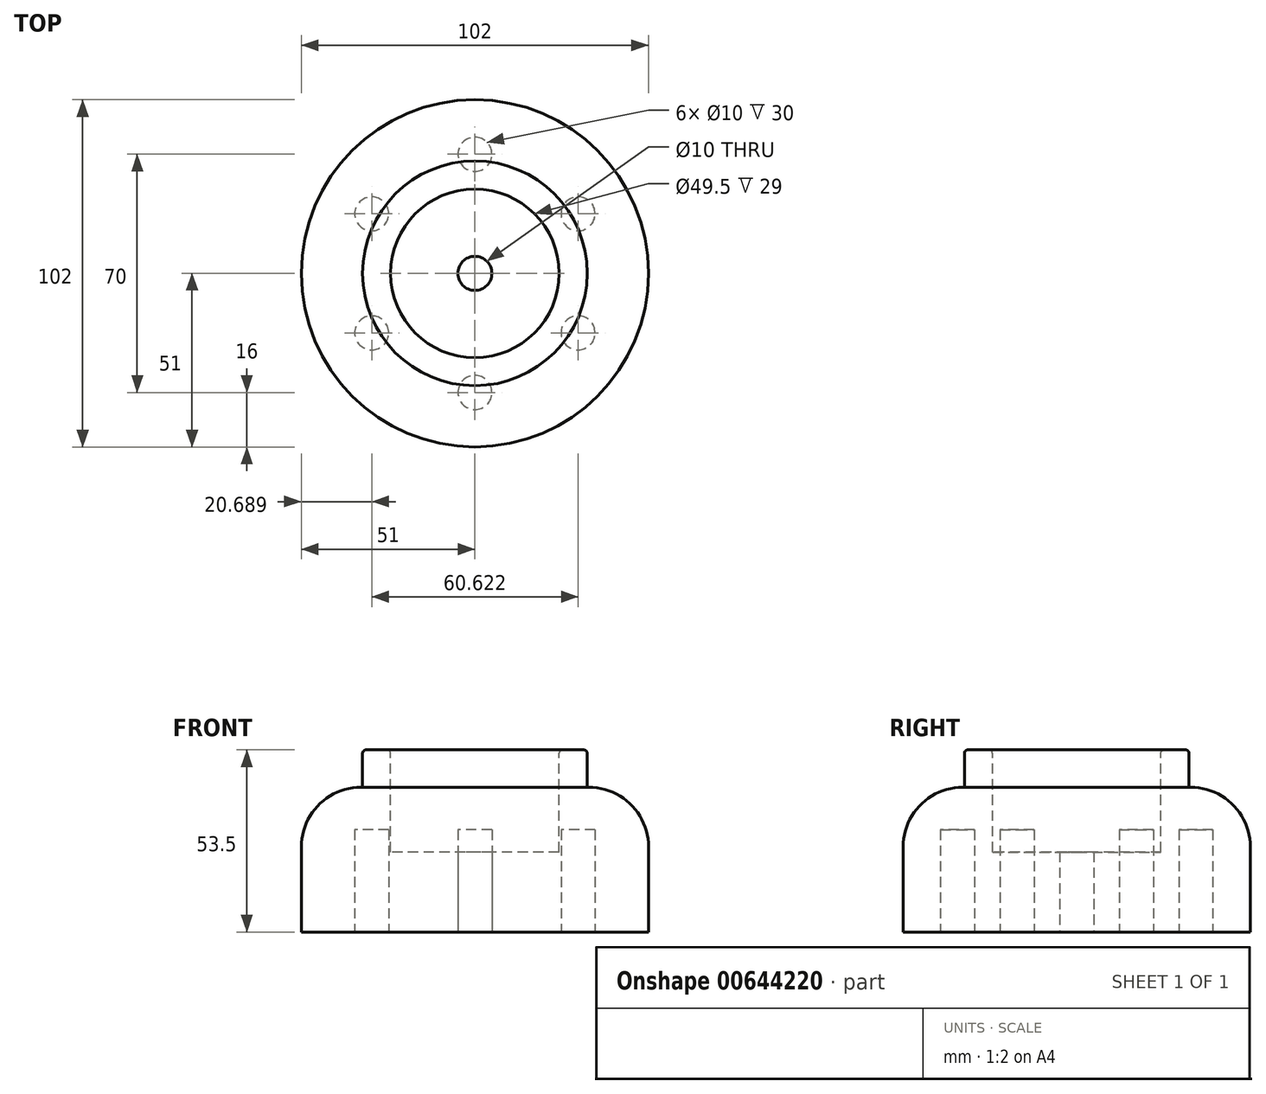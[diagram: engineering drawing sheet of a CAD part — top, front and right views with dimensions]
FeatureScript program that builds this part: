
annotation { "Feature Type Name" : "Feature", "Feature Type Description" : "" }
export const myFeature = defineFeature(function(context is Context, id is Id, definition is map)
    precondition{}
    {
        {
            var Q0;
            Q0=qCreatedBy(makeId("Top.planeOp"),FACE);
            var sketch = newSketch(context, id + "F0", { "sketchPlane" : qUnion([Q0])});
            skCircle(sketch, "E0", {"center": v(0, 0) * mm, "radius": 51 * mm});
            skSolve(sketch);
        }
        {
            var Q0;
            Q0=makeQuery(id+"F0.imprint","IMPRINT",FACE,{"disambiguationData":[TD([[makeQuery(id+"F0.imprint","IMPRINT",EDGE,{"derivedFrom":sQuery(id+"F0.wireOp",EDGE,"E0")}),1.0]])]});
            extrude(context, id + "F1", {"entities" : qUnion([Q0]), "depth" : 42.5 * mm});
        }
        {
            var Q0;
            Q0=makeQuery(id+"F1.opExtrude","CAP_EDGE",EDGE,{"disambiguationData":[OSD([sQuery(id+"F0.wireOp",EDGE,"E0")])],"isStart":false});
            fillet(context, id + "F2", {"entities" : qUnion([Q0]), "radius" : 17.5 * mm, "tangentPropagation" : true, "allowEdgeOverflow" : false});
        }
        {
            var Q0;
            Q0=qCreatedBy(makeId("Top.planeOp"),FACE);
            var sketch = newSketch(context, id + "F3", { "sketchPlane" : qUnion([Q0])});
            skCircle(sketch, "E1", {"center": v(0, 0) * mm, "radius": 5 * mm});
            skLineSegment(sketch, "E2", {"start": v(0, 0) * mm, "end": v(0, -35) * mm});
            skCircle(sketch, "E3", {"center": v(0, -35) * mm, "radius": 5 * mm});
            skCircle(sketch, "E4.1.0", {"center": v(30.31, -17.5) * mm, "radius": 5 * mm});
            skCircle(sketch, "E4.2.0", {"center": v(30.31, 17.5) * mm, "radius": 5 * mm});
            skCircle(sketch, "E4.3.0", {"center": v(0, 35) * mm, "radius": 5 * mm});
            skCircle(sketch, "E4.4.0", {"center": v(-30.31, 17.5) * mm, "radius": 5 * mm});
            skCircle(sketch, "E4.5.0", {"center": v(-30.31, -17.5) * mm, "radius": 5 * mm});
            skSolve(sketch);
        }
        {
            var Q0;
            Q0=makeQuery(id+"F3.imprint","IMPRINT",FACE,{"disambiguationData":[TD([[makeQuery(id+"F3.imprint","IMPRINT",EDGE,{"derivedFrom":sQuery(id+"F3.wireOp",EDGE,"E4.5.0")}),1.0]])]});
            var Q1;
            Q1=makeQuery(id+"F3.imprint","IMPRINT",FACE,{"disambiguationData":[TD([[makeQuery(id+"F3.imprint","IMPRINT",EDGE,{"derivedFrom":sQuery(id+"F3.wireOp",EDGE,"E3")}),1.0]])]});
            var Q2;
            Q2=makeQuery(id+"F3.imprint","IMPRINT",FACE,{"disambiguationData":[TD([[makeQuery(id+"F3.imprint","IMPRINT",EDGE,{"derivedFrom":sQuery(id+"F3.wireOp",EDGE,"E4.1.0")}),1.0]])]});
            var Q3;
            Q3=makeQuery(id+"F3.imprint","IMPRINT",FACE,{"disambiguationData":[TD([[makeQuery(id+"F3.imprint","IMPRINT",EDGE,{"derivedFrom":sQuery(id+"F3.wireOp",EDGE,"E4.2.0")}),1.0]])]});
            var Q4;
            Q4=makeQuery(id+"F3.imprint","IMPRINT",FACE,{"disambiguationData":[TD([[makeQuery(id+"F3.imprint","IMPRINT",EDGE,{"derivedFrom":sQuery(id+"F3.wireOp",EDGE,"E1")}),1.0]])]});
            var Q5;
            Q5=makeQuery(id+"F3.imprint","IMPRINT",FACE,{"disambiguationData":[TD([[makeQuery(id+"F3.imprint","IMPRINT",EDGE,{"derivedFrom":sQuery(id+"F3.wireOp",EDGE,"E4.3.0")}),1.0]])]});
            var Q6;
            Q6=makeQuery(id+"F3.imprint","IMPRINT",FACE,{"disambiguationData":[TD([[makeQuery(id+"F3.imprint","IMPRINT",EDGE,{"derivedFrom":sQuery(id+"F3.wireOp",EDGE,"E4.4.0")}),1.0]])]});
            extrude(context, id + "F4", {"entities" : qUnion([Q0, Q1, Q2, Q3, Q4, Q5, Q6]), "operationType" : NewBodyOperationType.REMOVE, "oppositeDirection" : true, "depth" : -30 * mm});
        }
        {
            var Q0;
            Q0=makeQuery(id+"F1.opExtrude","CAP_FACE",FACE,{"disambiguationData":[OSD([sQuery(id+"F0.wireOp",EDGE,"E0")])],"isStart":false});
            var sketch = newSketch(context, id + "F5", { "sketchPlane" : qUnion([Q0])});
            skCircle(sketch, "E5", {"center": v(0, 0) * mm, "radius": 33 * mm});
            skSolve(sketch);
        }
        {
            var Q0;
            Q0=makeQuery(id+"F5.imprint","IMPRINT",FACE,{"disambiguationData":[TD([[makeQuery(id+"F5.imprint","IMPRINT",EDGE,{"derivedFrom":sQuery(id+"F5.wireOp",EDGE,"E5")}),1.0]])]});
            extrude(context, id + "F6", {"entities" : qUnion([Q0]), "operationType" : NewBodyOperationType.ADD, "depth" : 11 * mm});
        }
        {
            var Q0;
            Q0=makeQuery(id+"F6.opExtrude","CAP_EDGE",EDGE,{"disambiguationData":[OSD([sQuery(id+"F5.wireOp",EDGE,"E5")])],"isStart":false});
            fillet(context, id + "F7", {"entities" : qUnion([Q0]), "radius" : 1 * mm, "tangentPropagation" : true, "allowEdgeOverflow" : false});
        }
        {
            var Q0;
            Q0=makeQuery(id+"F6.opExtrude","CAP_FACE",FACE,{"disambiguationData":[OSD([sQuery(id+"F5.wireOp",EDGE,"E5")])],"isStart":false});
            var sketch = newSketch(context, id + "F8", { "sketchPlane" : qUnion([Q0])});
            skCircle(sketch, "E6", {"center": v(0, 0) * mm, "radius": 24.75 * mm});
            skSolve(sketch);
        }
        {
            var Q0;
            Q0=makeQuery(id+"F8.imprint","IMPRINT",FACE,{"disambiguationData":[TD([[makeQuery(id+"F8.imprint","IMPRINT",EDGE,{"derivedFrom":sQuery(id+"F8.wireOp",EDGE,"E6")}),1.0]])]});
            extrude(context, id + "F9", {"entities" : qUnion([Q0]), "operationType" : NewBodyOperationType.REMOVE, "oppositeDirection" : true, "depth" : 30 * mm});
        }
        {
            var Q0;
            Q0=makeQuery(id+"F6.opExtrude","CAP_FACE",FACE,{"disambiguationData":[OSD([sQuery(id+"F5.wireOp",EDGE,"E5")])],"isStart":false});
            fillet(context, id + "F10", {"entities" : qUnion([Q0]), "radius" : 1 * mm, "tangentPropagation" : true, "allowEdgeOverflow" : false});
        }
    });
